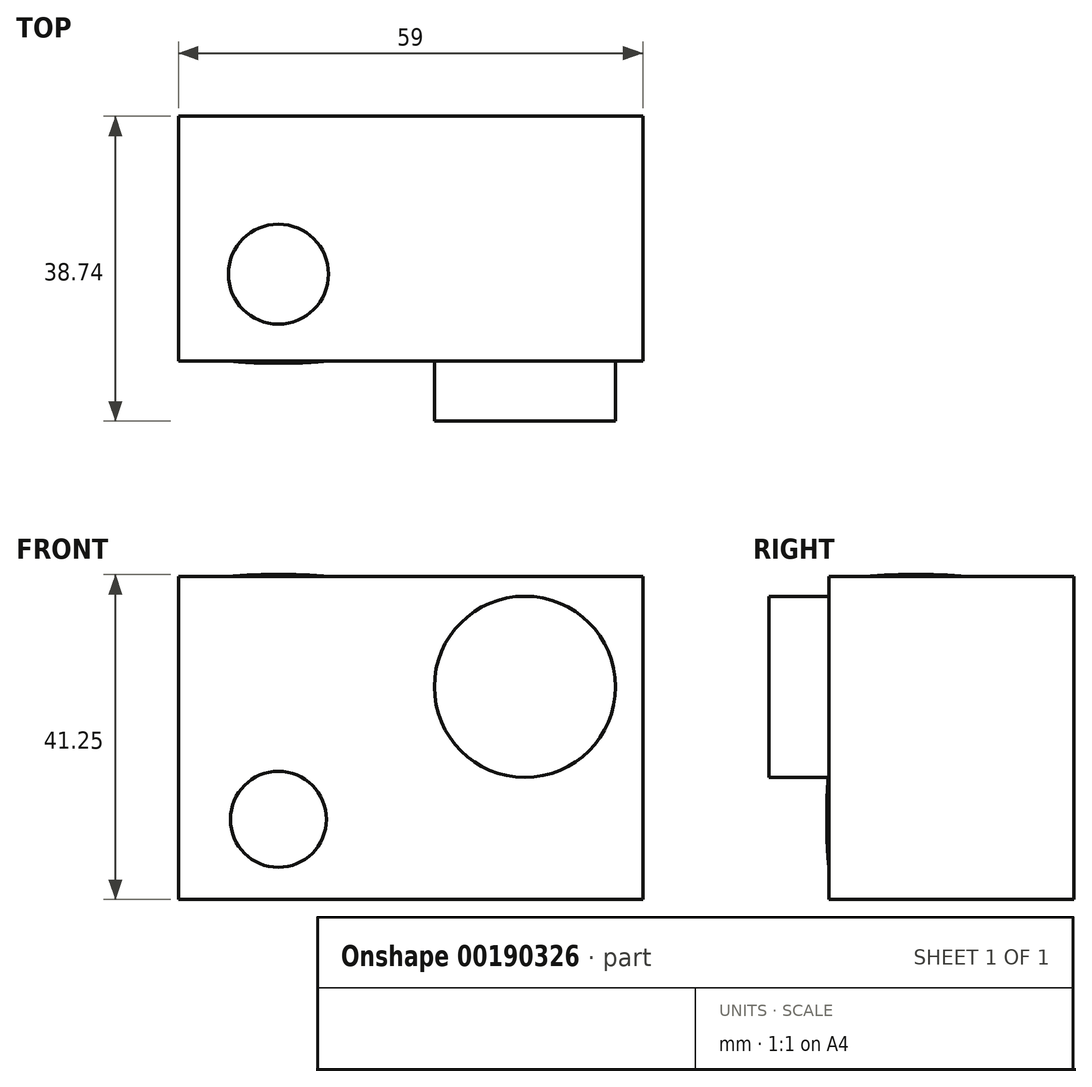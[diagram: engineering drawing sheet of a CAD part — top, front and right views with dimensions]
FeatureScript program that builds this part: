
annotation { "Feature Type Name" : "Feature", "Feature Type Description" : "" }
export const myFeature = defineFeature(function(context is Context, id is Id, definition is map)
    precondition{}
    {
        {
            var Q0;
            Q0=qCreatedBy(makeId("Front.planeOp"),FACE);
            var sketch = newSketch(context, id + "F0", { "sketchPlane" : qUnion([Q0])});
            skLineSegment(sketch, "E0.bottom", {"start": v(-50.44, 2.44) * mm, "end": v(8.56, 2.44) * mm});
            skLineSegment(sketch, "E0.top", {"start": v(-50.44, -38.55) * mm, "end": v(8.56, -38.55) * mm});
            skLineSegment(sketch, "E0.left", {"start": v(-50.44, 2.44) * mm, "end": v(-50.44, -38.55) * mm});
            skLineSegment(sketch, "E0.right", {"start": v(8.56, 2.44) * mm, "end": v(8.56, -38.55) * mm});
            skSolve(sketch);
        }
        {
            var Q0;
            Q0=makeQuery(id+"F0.imprint","IMPRINT",FACE,{"disambiguationData":[TD([[makeQuery(id+"F0.imprint","IMPRINT",EDGE,{"derivedFrom":sQuery(id+"F0.wireOp",EDGE,"E0.bottom")}),-1.0]])]});
            extrude(context, id + "F1", {"entities" : qUnion([Q0]), "depth" : 31.12 * mm});
        }
        {
            var Q0;
            Q0=makeQuery(id+"F1.opExtrude","CAP_FACE",FACE,{"disambiguationData":[OSD([sQuery(id+"F0.wireOp",EDGE,"E0.bottom"),sQuery(id+"F0.wireOp",EDGE,"E0.top"),sQuery(id+"F0.wireOp",EDGE,"E0.left"),sQuery(id+"F0.wireOp",EDGE,"E0.right")])],"isStart":false});
            var sketch = newSketch(context, id + "F2", { "sketchPlane" : qUnion([Q0])});
            skLineSegment(sketch, "E1", {"start": v(8.56, 2.44) * mm, "end": v(-6.42, 2.44) * mm});
            skLineSegment(sketch, "E2", {"start": v(-6.42, 2.44) * mm, "end": v(-6.42, -11.55) * mm});
            skSolve(sketch);
        }
        {
            var Q0;
            {var subQ2=sQuery(id+"F2.wireOp",EDGE,"E1");Q0=makeQuery(id+"F2.imprint","IMPRINT",FACE,{"disambiguationData":[TD([[makeQuery(id+"F2.imprint","IMPRINT",EDGE,{"derivedFrom":subQ2}),-1.0]])]});}
            var sketch = newSketch(context, id + "F3", { "sketchPlane" : qUnion([Q0])});
            skCircle(sketch, "E3", {"center": v(-6.42, -11.55) * mm, "radius": 11.5 * mm});
            skSolve(sketch);
        }
        {
            var Q0;
            Q0 = qSketchRegion(id + "F3", true);
            extrude(context, id + "F4", {"entities" : qUnion([Q0]), "operationType" : NewBodyOperationType.ADD, "depth" : 7.62 * mm});
        }
        {
            var Q0;
            {var subQ2=sQuery(id+"F2.wireOp",EDGE,"E1");Q0=makeQuery(id+"F2.imprint","IMPRINT",FACE,{"disambiguationData":[TD([[makeQuery(id+"F2.imprint","IMPRINT",EDGE,{"derivedFrom":subQ2}),-1.0]])]});}
            var sketch = newSketch(context, id + "F5", { "sketchPlane" : qUnion([Q0])});
            skLineSegment(sketch, "E4", {"start": v(-50.44, -38.55) * mm, "end": v(-37.74, -38.55) * mm});
            skLineSegment(sketch, "E5", {"start": v(-37.74, -38.55) * mm, "end": v(-37.74, -28.4) * mm});
            skSolve(sketch);
        }
        {
            var Q0;
            {var subQ2=sQuery(id+"F2.wireOp",EDGE,"E1");Q0=makeQuery(id+"F2.imprint","IMPRINT",FACE,{"disambiguationData":[TD([[makeQuery(id+"F2.imprint","IMPRINT",EDGE,{"derivedFrom":subQ2}),-1.0]])]});}
            var sketch = newSketch(context, id + "F6", { "sketchPlane" : qUnion([Q0])});
            skCircle(sketch, "E6", {"center": v(-37.74, -28.4) * mm, "radius": 6.1 * mm});
            skSolve(sketch);
        }
        {
            var Q0;
            Q0=makeQuery(id+"F6.imprint","IMPRINT",FACE,{"disambiguationData":[TD([[makeQuery(id+"F6.imprint","IMPRINT",EDGE,{"derivedFrom":sQuery(id+"F6.wireOp",EDGE,"E6")}),1.0]])]});
            extrude(context, id + "F7", {"entities" : qUnion([Q0]), "operationType" : NewBodyOperationType.ADD, "depth" : 0.25 * mm});
        }
        {
            var Q0;
            Q0=makeQuery(id+"F7.opExtrude","CAP_FACE",FACE,{"disambiguationData":[OSD([sQuery(id+"F6.wireOp",EDGE,"E6")])],"isStart":false});
            fillet(context, id + "F8", {"entities" : qUnion([Q0]), "radius" : 50.8 * mm, "tangentPropagation" : true, "allowEdgeOverflow" : false});
        }
        {
            var Q0;
            Q0=makeQuery(id+"F1.opExtrude","SWEPT_FACE",FACE,{"disambiguationData":[OSD([sQuery(id+"F0.wireOp",EDGE,"E0.bottom")])]});
            var sketch = newSketch(context, id + "F9", { "sketchPlane" : qUnion([Q0])});
            skLineSegment(sketch, "E7", {"start": v(-50.44, -31.12) * mm, "end": v(-37.74, -31.12) * mm});
            skLineSegment(sketch, "E8", {"start": v(-37.74, -31.12) * mm, "end": v(-37.74, -20.07) * mm});
            skSolve(sketch);
        }
        {
            var Q0;
            {var subQ2=sQuery(id+"F9.wireOp",EDGE,"E7");Q0=makeQuery(id+"F9.imprint","IMPRINT",FACE,{"disambiguationData":[TD([[makeQuery(id+"F9.imprint","IMPRINT",EDGE,{"derivedFrom":subQ2}),1.0]])]});}
            var sketch = newSketch(context, id + "F10", { "sketchPlane" : qUnion([Q0])});
            skCircle(sketch, "E9", {"center": v(-37.74, -20.07) * mm, "radius": 6.35 * mm});
            skSolve(sketch);
        }
        {
            var Q0;
            Q0=makeQuery(id+"F10.imprint","IMPRINT",FACE,{"disambiguationData":[TD([[makeQuery(id+"F10.imprint","IMPRINT",EDGE,{"derivedFrom":sQuery(id+"F10.wireOp",EDGE,"E9")}),1.0]])]});
            extrude(context, id + "F11", {"entities" : qUnion([Q0]), "operationType" : NewBodyOperationType.ADD, "depth" : 0.25 * mm});
        }
        {
            var Q0;
            Q0=makeQuery(id+"F11.opExtrude","CAP_EDGE",EDGE,{"disambiguationData":[OSD([sQuery(id+"F10.wireOp",EDGE,"E9")])],"isStart":false});
            fillet(context, id + "F12", {"entities" : qUnion([Q0]), "radius" : 50.8 * mm, "tangentPropagation" : true, "allowEdgeOverflow" : false});
        }
    });
